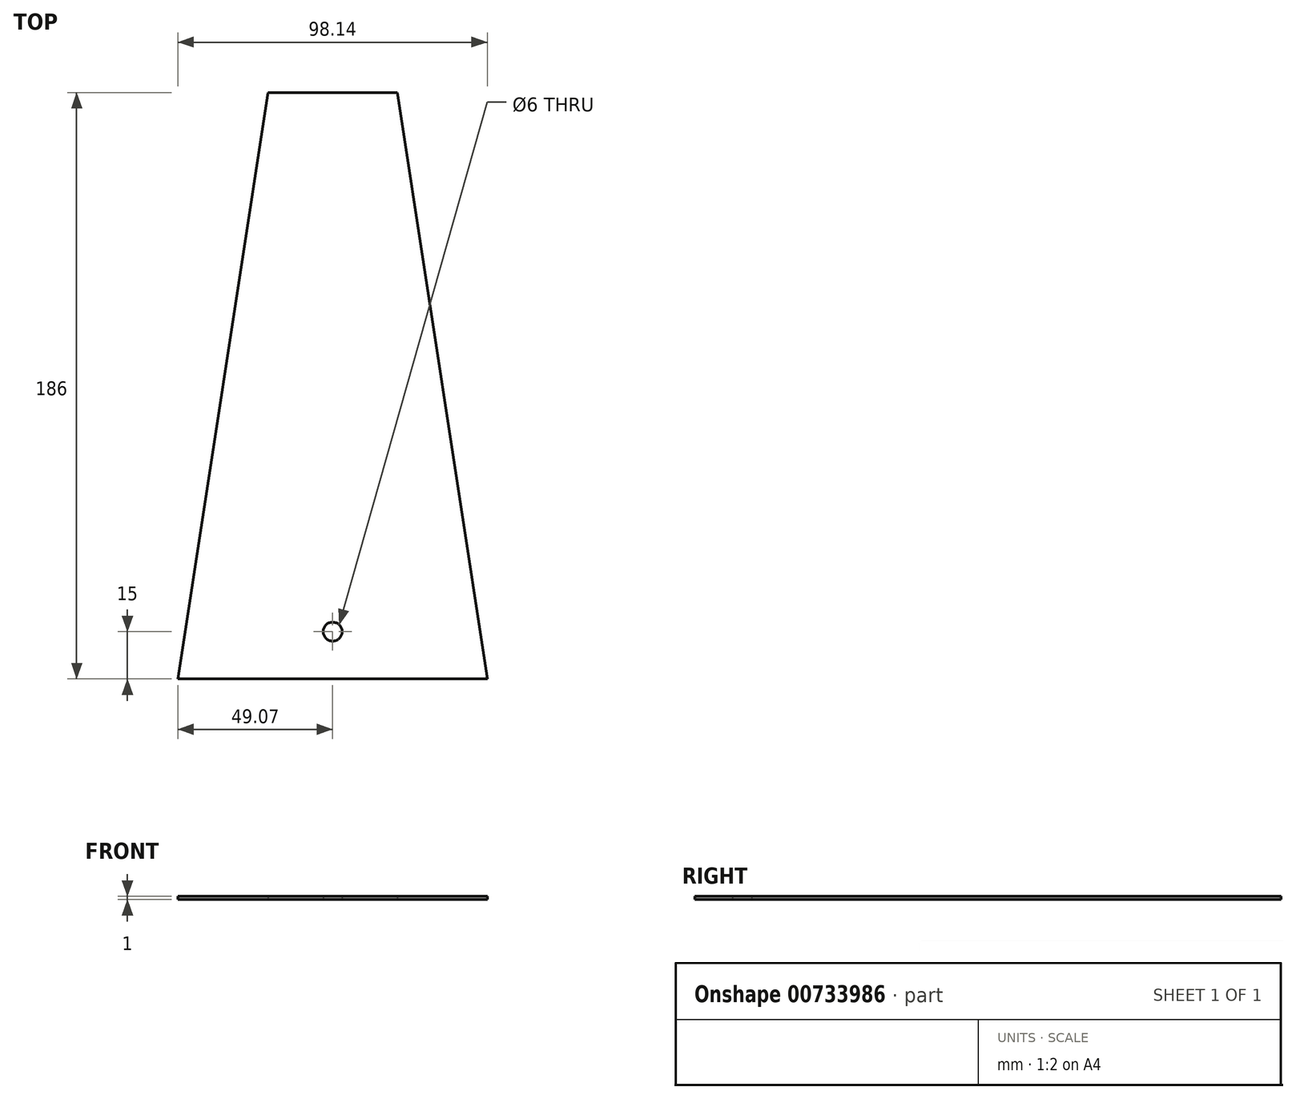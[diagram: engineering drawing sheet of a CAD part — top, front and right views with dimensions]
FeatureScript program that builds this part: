
annotation { "Feature Type Name" : "Feature", "Feature Type Description" : "" }
export const myFeature = defineFeature(function(context is Context, id is Id, definition is map)
    precondition{}
    {
        {
            var Q0;
            Q0=qCreatedBy(makeId("Top.planeOp"),FACE);
            var sketch = newSketch(context, id + "F0", { "sketchPlane" : qUnion([Q0])});
            skLineSegment(sketch, "E0", {"start": v(-46, 0) * mm, "end": v(-20.5, 166) * mm});
            skLineSegment(sketch, "E1", {"start": v(-20.5, 166) * mm, "end": v(20.5, 166) * mm});
            skLineSegment(sketch, "E2", {"start": v(20.5, 166) * mm, "end": v(49.07, -20) * mm});
            skLineSegment(sketch, "E3", {"start": v(46, 0) * mm, "end": v(-46, 0) * mm, "construction": true});
            skLineSegment(sketch, "E4", {"start": v(0, 166) * mm, "end": v(0, 0) * mm, "construction": true});
            skLineSegment(sketch, "E5", {"start": v(-46, 0) * mm, "end": v(-49.07, -20) * mm});
            skLineSegment(sketch, "E6", {"start": v(-49.07, -20) * mm, "end": v(49.07, -20) * mm});
            skCircle(sketch, "E7", {"center": v(0, -5) * mm, "radius": 3 * mm});
            skSolve(sketch);
        }
        {
            var Q0;
            Q0=qSketchRegion(id+"F0",true);
            extrude(context, id + "F1", {"entities" : qUnion([Q0]), "depth" : 1 * mm, "offsetDistance" : 25 * mm});
        }
    });
